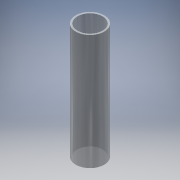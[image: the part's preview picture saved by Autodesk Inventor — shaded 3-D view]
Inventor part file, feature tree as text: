
AUTODESK INVENTOR PART (.ipt)
format: ipt  version: 2016 (Build 200138000, 138)  size: 101,376 bytes
history: native  units: in
note: dims shown in document units (in); Inventor stores cm internally (conversion verified against a paired STEP export)
features: extrude x1, sketch x1
ambient origin geometry x8: Origin, YZ Plane, XZ Plane, XY Plane, X Axis, Y Axis, Z Axis, Center Point
bodies: Solid1 (feature_tree)
feature tree (2):
  extrude  "Extrusion1"  Depth=14.1732in
  sketch  "Sketch1"  dims[d0=3.5in d1=0.216in d2=14.1732in d3=0.0in]
